# Revit family: FT Orion_2021
name_source: partatom
category: Luminarias
units: mm (PartAtom-declared; Revit-internal decimal feet)

## family parameters
Compartido = No
Corte con vacíos al cargar = No
Cota de conector redondo = Diámetro de uso
Número OmniClass = 23.80.70.00
Origen de luz = Sí
Punto de cálculo de habitación = No
Se basa en plano de trabajo = No
Siempre vertical = Sí
Tipo de pieza = Normal
Título OmniClass = Lighting

## types (12) — shared parameters
Cambio de temperatura de color de luz atenuada = <Ninguno>
Chromatic Index = CR>80
Descripción = https://www.airfal.com
Emergency system = No
Filtro de color = 16777215
Glow wire test = 850ºC
IK = IK09
IP = IP67
Led Module = Sí
Longitud de línea de emisión = 609.6 mm  [stored 2 ft]
MacAdam Ellipse = 3/4
Photobiological risk group = RG 0/1
URL = https://www.airfal.com
Unify glade rating = UGR<19
Useful life = L70B50>100000
Ángulo de inclinación = 90.00°
zero-valued in all types: Elevación por defecto

## per-type parameters (varying)
| type | Archivo de red fotométrica | L | Net output | Size | Watts |
| OR113 | OR113 600 13w 3000K 1490Lm.IES | 770 mm  [stored 2.52625 ft] | 1040 lm | 600 mm | 13 W |
| OR114 | OR114 13w 4000K 1550Lm.IES | 770 mm  [stored 2.52625 ft] | 1082 lm | 600 mm | 13 W |
| OR123 | OR123 600 16W 3000K 2560lm.IES | 770 mm  [stored 2.52625 ft] | 1787 lm | 600 mm | 16 W |
| OR124 | OR124 600 16W 4000K 2670lm.IES | 770 mm  [stored 2.52625 ft] | 1864 lm | 600 mm | 16 W |
| OR213 | PE213 PEGASO 1200 24W 2980 lm 3000ºK.IES | 1380 mm  [stored 4.52756 ft] | 2080 lm | 1200 mm | 24 W |
| OR214 | OR214 1200 24W 4000 3200lm.IES | 1380 mm  [stored 4.52756 ft] | 2234 lm | 1200 mm | 24 W |
| OR223 | OR223 1200 32W 3000 5120lm.IES | 1380 mm  [stored 4.52756 ft] | 3574 lm | 1200 mm | 32 W |
| OR313 | OR313 1500 29W 3000 3720lm.IES | 1633 mm  [stored 5.35761 ft] | 2597 lm | 1500 mm  [stored 4.92126 ft] | 29 W |
| OR224 | OR224 1200 32W 4000 5340lm.IES | 1380 mm  [stored 4.52756 ft] | 3727 lm | 1200 mm | 32 W |
| OR314 | OR314 1500 29W 4000 4000lm.IES | 1633 mm  [stored 5.35761 ft] | 2792 lm | 1500 mm  [stored 4.92126 ft] | 29 W |
| OR323 | OR323 1500 40W 3000 6310lm.IES | 1633 mm  [stored 5.35761 ft] | 4404 lm | 1500 mm  [stored 4.92126 ft] | 40 W |
| OR324 | OR324 1500 40W 4000 6700lm.IES | 1633 mm  [stored 5.35761 ft] | 4677 lm | 1500 mm  [stored 4.92126 ft] | 40 W |

note: [stored X ft] marks values corroborated as IEEE doubles in the binary element streams (Revit-internal decimal feet)

## geometry (parser evidence)
native form markers: Blend x2, Sweep x18
no freeform markers — native parametric forms only
